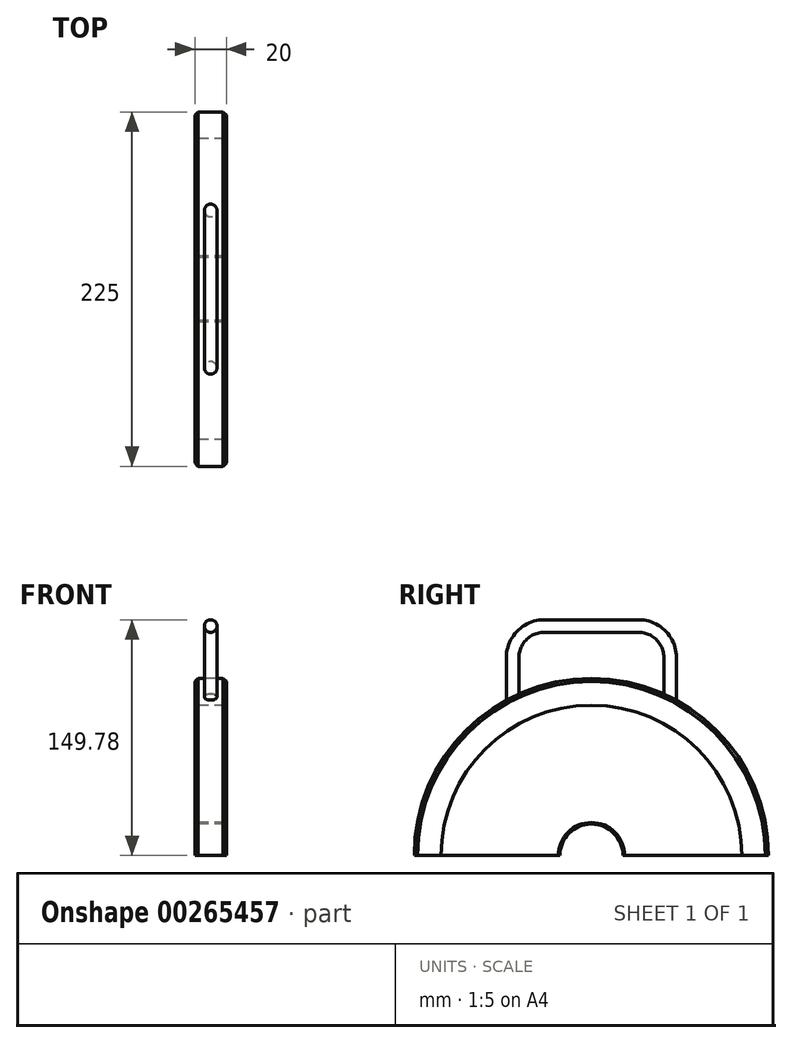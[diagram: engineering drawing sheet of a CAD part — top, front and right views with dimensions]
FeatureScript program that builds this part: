
annotation { "Feature Type Name" : "Feature", "Feature Type Description" : "" }
export const myFeature = defineFeature(function(context is Context, id is Id, definition is map)
    precondition{}
    {
        {
            var Q0;
            Q0=qCreatedBy(makeId("Front.planeOp"),FACE);
            var sketch = newSketch(context, id + "F0", { "sketchPlane" : qUnion([Q0])});
            skLineSegment(sketch, "E0", {"start": v(-48.97, 0) * mm, "end": v(48.97, 0) * mm, "construction": true});
            skLineSegment(sketch, "E1.bottom", {"start": v(-10, 21) * mm, "end": v(10, 21) * mm});
            skLineSegment(sketch, "E1.top", {"start": v(-10, 20) * mm, "end": v(10, 20) * mm});
            skLineSegment(sketch, "E1.left", {"start": v(-10, 21) * mm, "end": v(-10, 20) * mm});
            skLineSegment(sketch, "E1.right", {"start": v(10, 21) * mm, "end": v(10, 20) * mm});
            skLineSegment(sketch, "E2", {"start": v(0, 12.38) * mm, "end": v(0, -12.38) * mm, "construction": true});
            skSolve(sketch);
        }
        {
            var Q0;
            Q0=makeQuery(id+"F0.imprint","IMPRINT",FACE,{"disambiguationData":[TD([[makeQuery(id+"F0.imprint","IMPRINT",EDGE,{"derivedFrom":sQuery(id+"F0.wireOp",EDGE,"E1.bottom")}),-1.0]])]});
            var Q1;
            Q1=sQuery(id+"F0.wireOp",EDGE,"E0");
            revolve(context, id + "F1", {"entities" : qUnion([Q0]), "axis" : qUnion([Q1]), "revolveType" : RevolveType.FULL});
        }
        {
            var Q0;
            Q0=qCreatedBy(makeId("Front.planeOp"),FACE);
            var sketch = newSketch(context, id + "F2", { "sketchPlane" : qUnion([Q0])});
            skLineSegment(sketch, "E3.bottom", {"start": v(-10, 95.5) * mm, "end": v(10, 95.5) * mm});
            skLineSegment(sketch, "E3.top", {"start": v(-10, 21) * mm, "end": v(10, 21) * mm});
            skLineSegment(sketch, "E3.left", {"start": v(-10, 95.5) * mm, "end": v(-10, 21) * mm});
            skLineSegment(sketch, "E3.right", {"start": v(10, 95.5) * mm, "end": v(10, 21) * mm});
            skLineSegment(sketch, "E4", {"start": v(-46.04, 0) * mm, "end": v(46.04, 0) * mm, "construction": true});
            skSolve(sketch);
        }
        {
            var Q0;
            Q0=makeQuery(id+"F2.imprint","IMPRINT",FACE,{"disambiguationData":[TD([[makeQuery(id+"F2.imprint","IMPRINT",EDGE,{"derivedFrom":sQuery(id+"F2.wireOp",EDGE,"E3.bottom")}),-1.0]])]});
            var Q1;
            Q1=sQuery(id+"F2.wireOp",EDGE,"E4");
            revolve(context, id + "F3", {"entities" : qUnion([Q0]), "axis" : qUnion([Q1]), "revolveType" : RevolveType.FULL});
        }
        {
            var Q0;
            Q0=qCreatedBy(makeId("Front.planeOp"),FACE);
            var sketch = newSketch(context, id + "F4", { "sketchPlane" : qUnion([Q0])});
            skLineSegment(sketch, "E5", {"start": v(-40.4, 0) * mm, "end": v(40.4, 0) * mm, "construction": true});
            skLineSegment(sketch, "E6.bottom", {"start": v(-10, 112.5) * mm, "end": v(10, 112.5) * mm});
            skLineSegment(sketch, "E6.top", {"start": v(-10, 95.5) * mm, "end": v(10, 95.5) * mm});
            skLineSegment(sketch, "E6.left", {"start": v(-10, 112.5) * mm, "end": v(-10, 95.5) * mm});
            skLineSegment(sketch, "E6.right", {"start": v(10, 112.5) * mm, "end": v(10, 95.5) * mm});
            skSolve(sketch);
        }
        {
            var Q0;
            Q0=makeQuery(id+"F4.imprint","IMPRINT",FACE,{"disambiguationData":[TD([[makeQuery(id+"F4.imprint","IMPRINT",EDGE,{"derivedFrom":sQuery(id+"F4.wireOp",EDGE,"E6.bottom")}),-1.0]])]});
            var Q1;
            Q1=sQuery(id+"F4.wireOp",EDGE,"E5");
            revolve(context, id + "F5", {"entities" : qUnion([Q0]), "axis" : qUnion([Q1]), "revolveType" : RevolveType.FULL});
        }
        {
            var Q0;
            Q0=qCreatedBy(makeId("Right.planeOp"),FACE);
            var sketch = newSketch(context, id + "F6", { "sketchPlane" : qUnion([Q0])});
            skLineSegment(sketch, "E7", {"start": v(-50, 95.16) * mm, "end": v(-50, 125.78) * mm});
            skLineSegment(sketch, "E8", {"start": v(-30, 145.78) * mm, "end": v(30, 145.78) * mm});
            skLineSegment(sketch, "E9", {"start": v(50, 125.78) * mm, "end": v(50, 95.16) * mm});
            skPoint(sketch, "E10.visualSharp", {"position": v(50, 145.78) * mm});
            skArc(sketch, "E10.filletArc", {"start": v(50, 125.78) * mm, "mid": v(44.14, 139.92) * mm, "end": v(30, 145.78) * mm});
            skPoint(sketch, "E11.visualSharp", {"position": v(-50, 145.78) * mm});
            skArc(sketch, "E11.filletArc", {"start": v(-30, 145.78) * mm, "mid": v(-44.14, 139.92) * mm, "end": v(-50, 125.78) * mm});
            skPoint(sketch, "E12", {"position": v(50, 100.78) * mm});
            skSolve(sketch);
        }
        {
            var Q0;
            Q0=qCreatedBy(makeId("Top.planeOp"),FACE);
            var Q1;
            Q1=sQuery(id+"F6.wireOp",VERTEX,"E7.start");
            cPlane(context, id + "F7", {"entities" : qUnion([Q0, Q1]), "cplaneType" : CPlaneType.PLANE_POINT, "offset" : 25 * mm, "width" : 150 * mm, "height" : 150 * mm});
        }
        {
            var Q0;
            Q0=qCreatedBy(id+"F7.planeOp",FACE);
            var sketch = newSketch(context, id + "F8", { "sketchPlane" : qUnion([Q0])});
            skCircle(sketch, "E13", {"center": v(0, -50) * mm, "radius": 4 * mm});
            skSolve(sketch);
        }
        {
            var Q0;
            Q0=makeQuery(id+"F8.imprint","IMPRINT",FACE,{"disambiguationData":[TD([[makeQuery(id+"F8.imprint","IMPRINT",EDGE,{"derivedFrom":sQuery(id+"F8.wireOp",EDGE,"E13")}),1.0]])]});
            var Q1;
            Q1=sQuery(id+"F6.wireOp",EDGE,"E7");
            var Q2;
            Q2=sQuery(id+"F6.wireOp",EDGE,"E11.filletArc");
            var Q3;
            Q3=sQuery(id+"F6.wireOp",EDGE,"E8");
            var Q4;
            Q4=sQuery(id+"F6.wireOp",EDGE,"E10.filletArc");
            var Q5;
            Q5=sQuery(id+"F6.wireOp",EDGE,"E9");
            sweep(context, id + "F9", {"operationType" : NewBodyOperationType.ADD, "profiles" : qUnion([Q0]), "path" : qUnion([Q1, Q2, Q3, Q4, Q5])});
        }
        {
            var Q0;
            Q0=makeQuery(id+"F5.opRevolve","SWEPT_EDGE",EDGE,{"disambiguationData":[OSD([sQuery(id+"F4.wireOp",EDGE,"E6.bottom"),sQuery(id+"F4.wireOp",EDGE,"E6.right")])]});
            var Q1;
            Q1=makeQuery(id+"F5.opRevolve","SWEPT_EDGE",EDGE,{"disambiguationData":[OSD([sQuery(id+"F4.wireOp",EDGE,"E6.bottom"),sQuery(id+"F4.wireOp",EDGE,"E6.left")])]});
            chamfer(context, id + "F10", {"entities" : qUnion([Q0, Q1]), "width" : 2 * mm, "tangentPropagation" : true});
        }
        {
            var Q0;
            Q0=qCreatedBy(makeId("Front.planeOp"),FACE);
            var sketch = newSketch(context, id + "F11", { "sketchPlane" : qUnion([Q0])});
            skLineSegment(sketch, "E14.bottom", {"start": v(-10, 0) * mm, "end": v(10, 0) * mm});
            skLineSegment(sketch, "E14.top", {"start": v(-10, -115) * mm, "end": v(10, -115) * mm});
            skLineSegment(sketch, "E14.left", {"start": v(-10, 0) * mm, "end": v(-10, -115) * mm});
            skLineSegment(sketch, "E14.right", {"start": v(10, 0) * mm, "end": v(10, -115) * mm});
            skSolve(sketch);
        }
        {
            var Q0;
            Q0=qSketchRegion(id+"F11",true);
            extrude(context, id + "F12", {"entities" : qUnion([Q0]), "operationType" : NewBodyOperationType.REMOVE, "endBound" : BoundingType.THROUGH_ALL, "depth" : 25 * mm, "hasSecondDirection" : true, "secondDirectionBound" : SecondDirectionBoundingType.THROUGH_ALL, "secondDirectionOppositeDirection" : true, "secondDirectionDepth" : 25 * mm});
        }
    });
